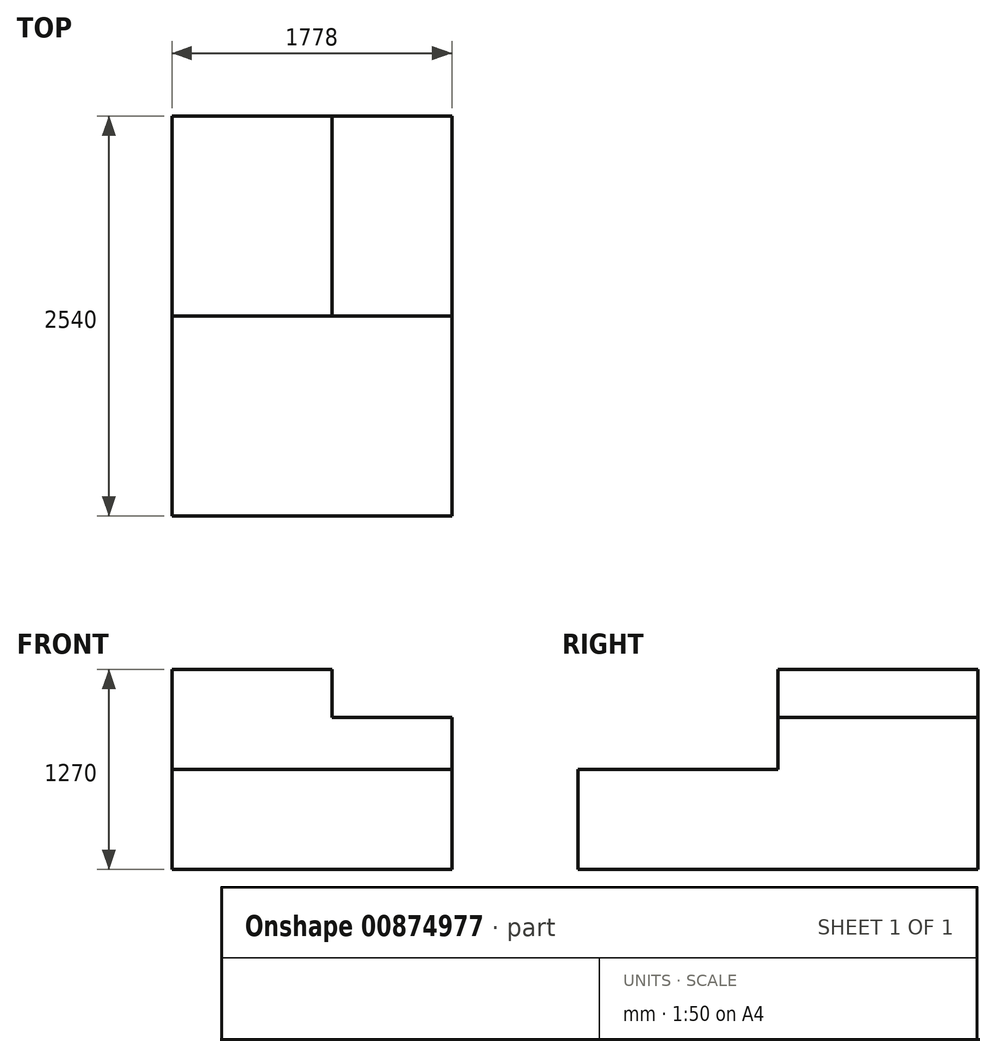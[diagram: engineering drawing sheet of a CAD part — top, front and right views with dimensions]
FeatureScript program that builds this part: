
annotation { "Feature Type Name" : "Feature", "Feature Type Description" : "" }
export const myFeature = defineFeature(function(context is Context, id is Id, definition is map)
    precondition{}
    {
        {
            var Q0;
            Q0=qCreatedBy(makeId("Top.planeOp"),FACE);
            var sketch = newSketch(context, id + "F0", { "sketchPlane" : qUnion([Q0])});
            skLineSegment(sketch, "E0", {"start": v(0, 0) * mm, "end": v(1778, 0) * mm});
            skLineSegment(sketch, "E1", {"start": v(1778, 0) * mm, "end": v(1778, 2540) * mm});
            skLineSegment(sketch, "E2", {"start": v(1778, 2540) * mm, "end": v(0, 2540) * mm});
            skLineSegment(sketch, "E3", {"start": v(0, 2540) * mm, "end": v(0, 0) * mm});
            skSolve(sketch);
        }
        {
            var Q0;
            Q0=makeQuery(id+"F0.imprint","IMPRINT",FACE,{"disambiguationData":[TD([[makeQuery(id+"F0.imprint","IMPRINT",EDGE,{"derivedFrom":sQuery(id+"F0.wireOp",EDGE,"E0")}),1.0]])]});
            extrude(context, id + "F1", {"entities" : qUnion([Q0]), "depth" : 635 * mm, "offsetDistance" : 25.4 * mm});
        }
        {
            var Q0;
            Q0=makeQuery(id+"F1.opExtrude","CAP_FACE",FACE,{"disambiguationData":[OSD([sQuery(id+"F0.wireOp",EDGE,"E0"),sQuery(id+"F0.wireOp",EDGE,"E1"),sQuery(id+"F0.wireOp",EDGE,"E2"),sQuery(id+"F0.wireOp",EDGE,"E3")])],"isStart":false});
            var sketch = newSketch(context, id + "F2", { "sketchPlane" : qUnion([Q0])});
            skLineSegment(sketch, "E4", {"start": v(0, 2540) * mm, "end": v(0, 1270) * mm});
            skLineSegment(sketch, "E5", {"start": v(0, 1270) * mm, "end": v(1778, 1270) * mm});
            skLineSegment(sketch, "E6", {"start": v(1778, 1270) * mm, "end": v(1778, 2540) * mm});
            skLineSegment(sketch, "E7", {"start": v(1778, 2540) * mm, "end": v(0, 2540) * mm});
            skSolve(sketch);
        }
        {
            var Q0;
            Q0=makeQuery(id+"F2.imprint","IMPRINT",FACE,{"disambiguationData":[TD([[makeQuery(id+"F2.imprint","IMPRINT",EDGE,{"derivedFrom":sQuery(id+"F2.wireOp",EDGE,"E4")}),1.0]])]});
            extrude(context, id + "F3", {"entities" : qUnion([Q0]), "operationType" : NewBodyOperationType.ADD, "depth" : 330.2 * mm, "offsetDistance" : 25.4 * mm});
        }
        {
            var Q0;
            Q0=makeQuery(id+"F3.opExtrude","CAP_FACE",FACE,{"disambiguationData":[OSD([sQuery(id+"F2.wireOp",EDGE,"E4"),sQuery(id+"F2.wireOp",EDGE,"E5"),sQuery(id+"F2.wireOp",EDGE,"E6"),sQuery(id+"F2.wireOp",EDGE,"E7")])],"isStart":false});
            var sketch = newSketch(context, id + "F4", { "sketchPlane" : qUnion([Q0])});
            skLineSegment(sketch, "E8", {"start": v(0, 2540) * mm, "end": v(0, 1270) * mm});
            skLineSegment(sketch, "E9", {"start": v(0, 1270) * mm, "end": v(1016, 1270) * mm});
            skLineSegment(sketch, "E10", {"start": v(1016, 1270) * mm, "end": v(1016, 2540) * mm});
            skLineSegment(sketch, "E11", {"start": v(1016, 2540) * mm, "end": v(0, 2540) * mm});
            skSolve(sketch);
        }
        {
            var Q0;
            Q0=makeQuery(id+"F4.imprint","IMPRINT",FACE,{"disambiguationData":[TD([[makeQuery(id+"F4.imprint","IMPRINT",EDGE,{"derivedFrom":sQuery(id+"F4.wireOp",EDGE,"E8")}),1.0]])]});
            extrude(context, id + "F5", {"entities" : qUnion([Q0]), "operationType" : NewBodyOperationType.ADD, "depth" : 304.8 * mm, "offsetDistance" : 25.4 * mm});
        }
    });
